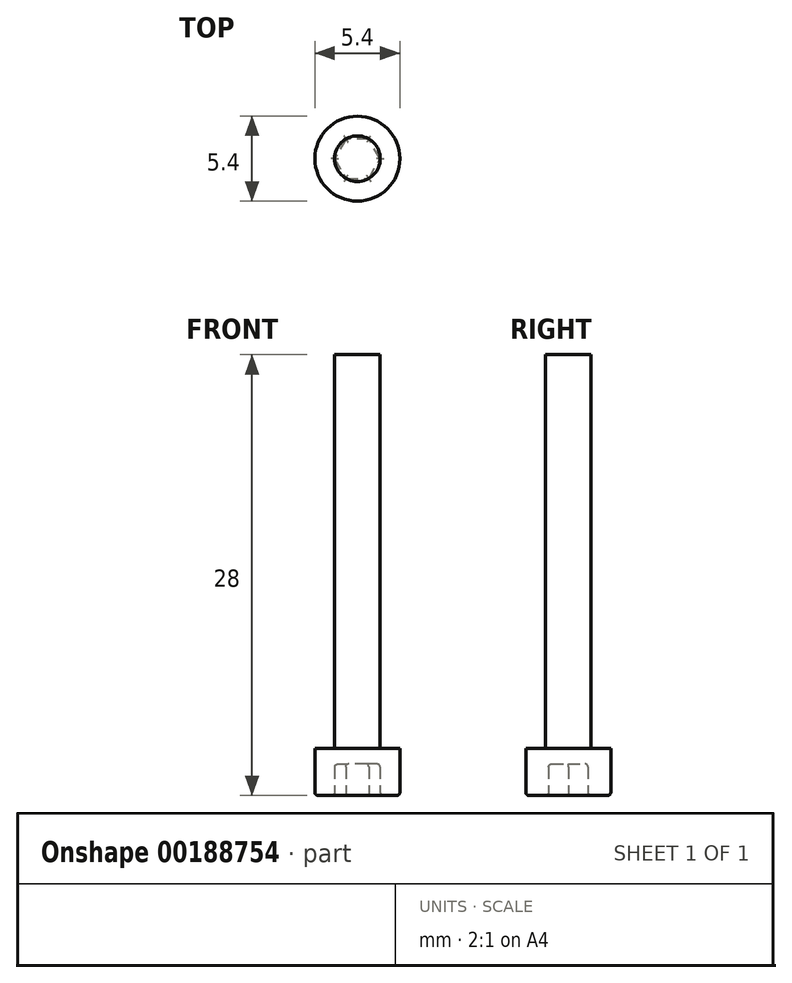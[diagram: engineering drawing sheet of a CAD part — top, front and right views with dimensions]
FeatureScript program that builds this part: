
annotation { "Feature Type Name" : "Feature", "Feature Type Description" : "" }
export const myFeature = defineFeature(function(context is Context, id is Id, definition is map)
    precondition{}
    {
        {
            var Q0;
            Q0=qCreatedBy(makeId("Top.planeOp"),FACE);
            var sketch = newSketch(context, id + "F0", { "sketchPlane" : qUnion([Q0])});
            skCircle(sketch, "E0", {"center": v(-51.4, -20.23) * mm, "radius": 2.7 * mm});
            skCircle(sketch, "E1", {"center": v(-51.4, -20.23) * mm, "radius": 1.45 * mm});
            skSolve(sketch);
        }
        {
            var Q0;
            Q0=makeQuery(id+"F0.imprint","IMPRINT",FACE,{"disambiguationData":[TD([[makeQuery(id+"F0.imprint","IMPRINT",EDGE,{"derivedFrom":sQuery(id+"F0.wireOp",EDGE,"E0")}),1.0]])]});
            var Q1;
            Q1=makeQuery(id+"F0.imprint","IMPRINT",FACE,{"disambiguationData":[TD([[makeQuery(id+"F0.imprint","IMPRINT",EDGE,{"derivedFrom":sQuery(id+"F0.wireOp",EDGE,"E1")}),1.0]])]});
            extrude(context, id + "F1", {"entities" : qUnion([Q0, Q1]), "depth" : 3 * mm, "offsetDistance" : 25 * mm});
        }
        {
            var Q0;
            Q0=makeQuery(id+"F0.imprint","IMPRINT",FACE,{"disambiguationData":[TD([[makeQuery(id+"F0.imprint","IMPRINT",EDGE,{"derivedFrom":sQuery(id+"F0.wireOp",EDGE,"E1")}),1.0]])]});
            extrude(context, id + "F2", {"entities" : qUnion([Q0]), "operationType" : NewBodyOperationType.ADD, "depth" : 28 * mm, "offsetDistance" : 25 * mm});
        }
        {
            var Q0;
            Q0=makeQuery(id+"F1.opExtrude","CAP_FACE",FACE,{"disambiguationData":[OSD([sQuery(id+"F0.wireOp",EDGE,"E0")])],"isStart":true});
            var sketch = newSketch(context, id + "F3", { "sketchPlane" : qUnion([Q0])});
            skCircle(sketch, "E2.cCircle", {"center": v(-51.4, 20.23) * mm, "radius": 1.25 * mm, "construction": true});
            skLineSegment(sketch, "E2.0", {"start": v(-50.69, 18.98) * mm, "end": v(-52.13, 18.98) * mm});
            skLineSegment(sketch, "E2.1", {"start": v(-52.13, 18.98) * mm, "end": v(-52.85, 20.23) * mm});
            skLineSegment(sketch, "E2.2", {"start": v(-52.85, 20.23) * mm, "end": v(-52.13, 21.48) * mm});
            skLineSegment(sketch, "E2.3", {"start": v(-52.13, 21.48) * mm, "end": v(-50.69, 21.48) * mm});
            skLineSegment(sketch, "E2.4", {"start": v(-50.69, 21.48) * mm, "end": v(-49.97, 20.23) * mm});
            skLineSegment(sketch, "E2.5", {"start": v(-49.97, 20.23) * mm, "end": v(-50.69, 18.98) * mm});
            skPoint(sketch, "E2.0.midPoint", {"position": v(-51.4, 18.98) * mm});
            skSolve(sketch);
        }
        {
            var Q0;
            Q0=makeQuery(id+"F3.imprint","IMPRINT",FACE,{"disambiguationData":[TD([[makeQuery(id+"F3.imprint","IMPRINT",EDGE,{"derivedFrom":sQuery(id+"F3.wireOp",EDGE,"E2.0")}),-1.0]])]});
            extrude(context, id + "F4", {"entities" : qUnion([Q0]), "operationType" : NewBodyOperationType.REMOVE, "oppositeDirection" : true, "depth" : 2 * mm, "offsetDistance" : 25 * mm});
        }
        {
            var Q0;
            Q0=makeQuery(id+"F1.opExtrude","CAP_EDGE",EDGE,{"disambiguationData":[OSD([sQuery(id+"F0.wireOp",EDGE,"E0")])],"isStart":true});
            var Q1;
            Q1=makeQuery(id+"F4.boolean.opBoolean","COPY",FACE,{"derivedFrom":makeQuery(id+"F4.opExtrude","CAP_FACE",FACE,{"disambiguationData":[OSD([sQuery(id+"F3.wireOp",EDGE,"E2.0"),sQuery(id+"F3.wireOp",EDGE,"E2.1"),sQuery(id+"F3.wireOp",EDGE,"E2.2"),sQuery(id+"F3.wireOp",EDGE,"E2.3"),sQuery(id+"F3.wireOp",EDGE,"E2.4"),sQuery(id+"F3.wireOp",EDGE,"E2.5")])],"isStart":false})});
            var Q2;
            Q2=makeQuery(id+"F1.opExtrude","CAP_FACE",FACE,{"disambiguationData":[OSD([sQuery(id+"F0.wireOp",EDGE,"E0")])],"isStart":true});
            fillet(context, id + "F5", {"entities" : qUnion([Q0, Q1, Q2]), "radius" : .2 * mm, "tangentPropagation" : true, "allowEdgeOverflow" : false});
        }
    });
